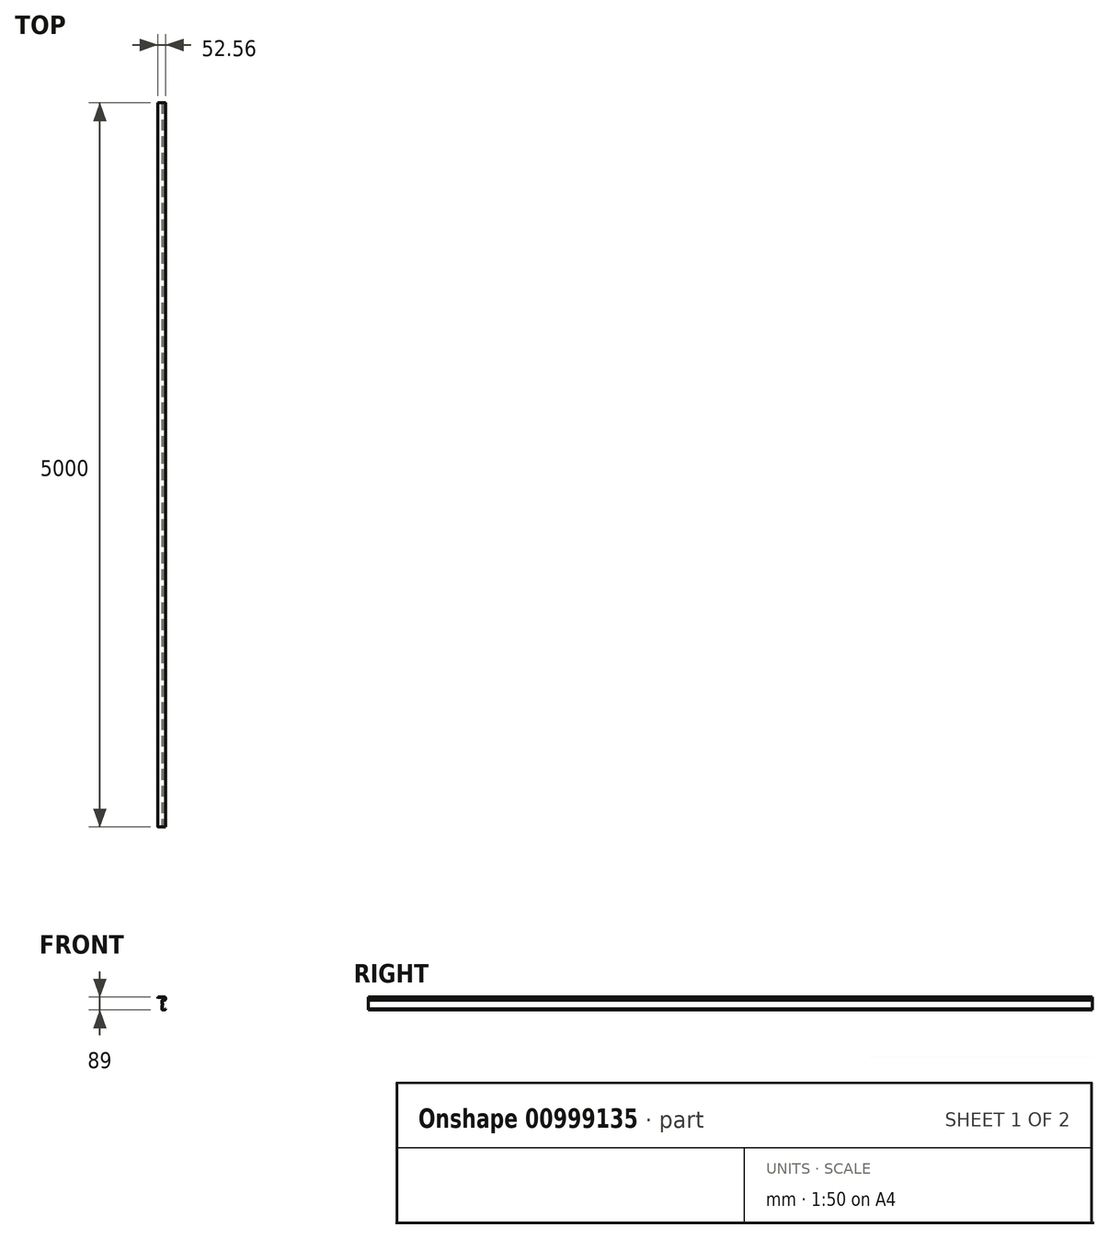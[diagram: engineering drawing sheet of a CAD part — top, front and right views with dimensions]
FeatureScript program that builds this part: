
annotation { "Feature Type Name" : "Feature", "Feature Type Description" : "" }
export const myFeature = defineFeature(function(context is Context, id is Id, definition is map)
    precondition{}
    {
        {
            var Q0;
            Q0=qCreatedBy(makeId("Front.planeOp"),FACE);
            var sketch = newSketch(context, id + "F0", { "sketchPlane" : qUnion([Q0])});
            skLineSegment(sketch, "E0", {"start": v(26.28, -36.18) * mm, "end": v(26.28, -40.2) * mm});
            skArc(sketch, "E1", {"start": v(4.12, 2.76) * mm, "mid": v(4.45, 1.09) * mm, "end": v(5.4, -0.33) * mm});
            skArc(sketch, "E2", {"start": v(5.4, -10.93) * mm, "mid": v(4.45, -12.35) * mm, "end": v(4.12, -14.03) * mm});
            skArc(sketch, "E3", {"start": v(4.42, -9.8) * mm, "mid": v(3.1, -11.79) * mm, "end": v(2.63, -14.13) * mm});
            skArc(sketch, "E4", {"start": v(2.63, 2.87) * mm, "mid": v(3.1, 0.53) * mm, "end": v(4.42, -1.46) * mm});
            skArc(sketch, "E5", {"start": v(6.6, -7.61) * mm, "mid": v(7.43, -5.63) * mm, "end": v(6.6, -3.65) * mm});
            skLineSegment(sketch, "E6", {"start": v(5.4, -0.33) * mm, "end": v(7.66, -2.6) * mm});
            skLineSegment(sketch, "E7", {"start": v(7.66, -8.67) * mm, "end": v(5.4, -10.93) * mm});
            skLineSegment(sketch, "E8", {"start": v(4.42, -9.8) * mm, "end": v(6.6, -7.61) * mm});
            skLineSegment(sketch, "E9", {"start": v(6.6, -3.65) * mm, "end": v(4.42, -1.46) * mm});
            skArc(sketch, "E10", {"start": v(6.92, 22.25) * mm, "mid": v(4.94, 21.43) * mm, "end": v(4.12, 19.44) * mm});
            skArc(sketch, "E11", {"start": v(21.99, -43.01) * mm, "mid": v(23.97, -42.19) * mm, "end": v(24.8, -40.2) * mm});
            skArc(sketch, "E12", {"start": v(4.12, -40.2) * mm, "mid": v(4.94, -42.19) * mm, "end": v(6.92, -43.01) * mm});
            skArc(sketch, "E13", {"start": v(21.99, 23.74) * mm, "mid": v(23.97, 24.56) * mm, "end": v(24.8, 26.54) * mm});
            skArc(sketch, "E14", {"start": v(24.8, 40.2) * mm, "mid": v(23.97, 42.19) * mm, "end": v(21.99, 43.01) * mm});
            skArc(sketch, "E15", {"start": v(-21.99, 43.01) * mm, "mid": v(-23.97, 42.19) * mm, "end": v(-24.8, 40.2) * mm});
            skLineSegment(sketch, "E16", {"start": v(-24.8, 36.18) * mm, "end": v(-26.28, 36.18) * mm});
            skLineSegment(sketch, "E17", {"start": v(-26.28, 36.18) * mm, "end": v(-26.28, 40.2) * mm});
            skLineSegment(sketch, "E18", {"start": v(-21.99, 44.5) * mm, "end": v(21.99, 44.5) * mm});
            skLineSegment(sketch, "E19", {"start": v(26.28, 40.2) * mm, "end": v(26.28, 26.54) * mm});
            skLineSegment(sketch, "E20", {"start": v(21.99, 22.25) * mm, "end": v(6.92, 22.25) * mm});
            skLineSegment(sketch, "E21", {"start": v(4.12, 19.44) * mm, "end": v(4.12, 2.76) * mm});
            skLineSegment(sketch, "E22", {"start": v(4.12, -14.03) * mm, "end": v(4.12, -30.6) * mm});
            skLineSegment(sketch, "E23", {"start": v(4.12, -14.03) * mm, "end": v(4.12, -40.2) * mm});
            skLineSegment(sketch, "E24", {"start": v(6.92, -43.01) * mm, "end": v(21.99, -43.01) * mm});
            skLineSegment(sketch, "E25", {"start": v(24.8, -40.2) * mm, "end": v(24.8, -36.18) * mm});
            skLineSegment(sketch, "E26", {"start": v(24.8, -36.18) * mm, "end": v(26.28, -36.18) * mm});
            skLineSegment(sketch, "E27", {"start": v(21.99, -44.5) * mm, "end": v(6.92, -44.5) * mm});
            skLineSegment(sketch, "E28", {"start": v(2.63, -40.2) * mm, "end": v(2.63, -14.13) * mm});
            skLineSegment(sketch, "E29", {"start": v(2.63, -30.5) * mm, "end": v(2.63, -14.13) * mm});
            skLineSegment(sketch, "E30", {"start": v(2.63, 2.87) * mm, "end": v(2.63, 19.44) * mm});
            skLineSegment(sketch, "E31", {"start": v(6.92, 23.74) * mm, "end": v(21.99, 23.74) * mm});
            skLineSegment(sketch, "E32", {"start": v(24.8, 26.54) * mm, "end": v(24.8, 40.2) * mm});
            skLineSegment(sketch, "E33", {"start": v(21.99, 43.01) * mm, "end": v(-21.99, 43.01) * mm});
            skLineSegment(sketch, "E34", {"start": v(-24.8, 40.2) * mm, "end": v(-24.8, 36.18) * mm});
            skArc(sketch, "E35", {"start": v(-21.99, 44.5) * mm, "mid": v(-25.02, 43.24) * mm, "end": v(-26.28, 40.2) * mm});
            skArc(sketch, "E36", {"start": v(26.28, 40.2) * mm, "mid": v(25.02, 43.24) * mm, "end": v(21.99, 44.5) * mm});
            skArc(sketch, "E37", {"start": v(21.99, 22.25) * mm, "mid": v(25.02, 23.5) * mm, "end": v(26.28, 26.54) * mm});
            skArc(sketch, "E38", {"start": v(6.92, 23.74) * mm, "mid": v(3.89, 22.48) * mm, "end": v(2.63, 19.44) * mm});
            skArc(sketch, "E39", {"start": v(7.66, -8.67) * mm, "mid": v(8.92, -5.63) * mm, "end": v(7.66, -2.6) * mm});
            skArc(sketch, "E40", {"start": v(2.63, -40.2) * mm, "mid": v(3.89, -43.24) * mm, "end": v(6.92, -44.5) * mm});
            skArc(sketch, "E41", {"start": v(21.99, -44.5) * mm, "mid": v(25.02, -43.24) * mm, "end": v(26.28, -40.2) * mm});
            skSolve(sketch);
        }
        {
            var Q0;
            Q0=makeQuery(id+"F0.imprint","IMPRINT",FACE,{"disambiguationData":[TD([[makeQuery(id+"F0.imprint","IMPRINT",EDGE,{"derivedFrom":sQuery(id+"F0.wireOp",EDGE,"E1")}),-1.0]])]});
            extrude(context, id + "F1", {"entities" : qUnion([Q0]), "oppositeDirection" : true, "depth" : 5000 * mm, "offsetDistance" : 25 * mm});
        }
    });
